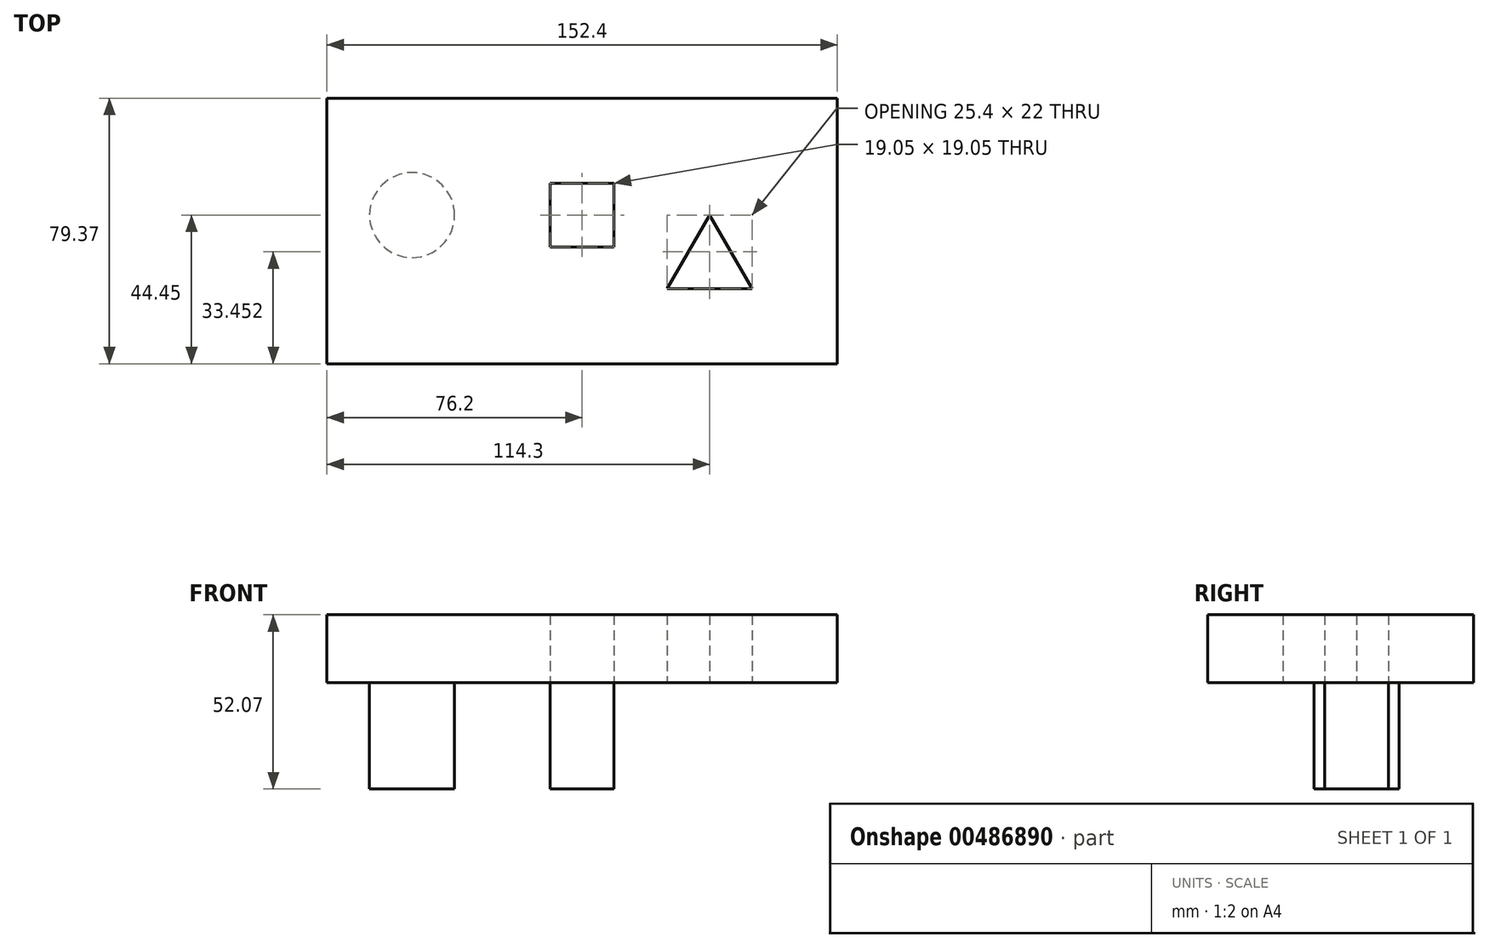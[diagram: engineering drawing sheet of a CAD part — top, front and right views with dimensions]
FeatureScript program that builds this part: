
annotation { "Feature Type Name" : "Feature", "Feature Type Description" : "" }
export const myFeature = defineFeature(function(context is Context, id is Id, definition is map)
    precondition{}
    {
        {
            var Q0;
            Q0=qCreatedBy(makeId("Top.planeOp"),FACE);
            var sketch = newSketch(context, id + "F0", { "sketchPlane" : qUnion([Q0])});
            skLineSegment(sketch, "E0", {"start": v(0, -44.45) * mm, "end": v(44.45, -44.45) * mm});
            skLineSegment(sketch, "E1.bottom", {"start": v(44.45, -44.45) * mm, "end": v(-107.95, -44.45) * mm});
            skLineSegment(sketch, "E1.top", {"start": v(44.45, 34.92) * mm, "end": v(-107.95, 34.92) * mm});
            skLineSegment(sketch, "E1.left", {"start": v(44.45, -44.45) * mm, "end": v(44.45, 34.92) * mm});
            skLineSegment(sketch, "E1.right", {"start": v(-107.95, -44.45) * mm, "end": v(-107.95, 34.92) * mm});
            skLineSegment(sketch, "E2", {"start": v(0, 0) * mm, "end": v(6.35, 0) * mm});
            skLineSegment(sketch, "E3", {"start": v(6.35, 0) * mm, "end": v(-6.35, -22) * mm});
            skLineSegment(sketch, "E4", {"start": v(-6.35, -22) * mm, "end": v(19.05, -22) * mm});
            skLineSegment(sketch, "E5", {"start": v(19.05, -22) * mm, "end": v(6.35, 0) * mm});
            skLineSegment(sketch, "E6", {"start": v(0, 0) * mm, "end": v(-31.75, 0) * mm});
            skLineSegment(sketch, "E7.bottom", {"start": v(-22.22, 9.53) * mm, "end": v(-41.27, 9.53) * mm});
            skLineSegment(sketch, "E7.top", {"start": v(-22.22, -9.53) * mm, "end": v(-41.27, -9.52) * mm});
            skLineSegment(sketch, "E7.left", {"start": v(-22.22, 9.53) * mm, "end": v(-22.22, -9.52) * mm});
            skLineSegment(sketch, "E7.right", {"start": v(-41.27, 9.53) * mm, "end": v(-41.27, -9.52) * mm});
            skPoint(sketch, "E7.middle", {"position": v(-31.75, 0) * mm});
            skCircle(sketch, "E8", {"center": v(-82.55, 0) * mm, "radius": 12.7 * mm});
            skSolve(sketch);
        }
        {
            var Q0;
            Q0=makeQuery(id+"F0.imprint","IMPRINT",FACE,{"disambiguationData":[TD([[makeQuery(id+"F0.imprint","IMPRINT",EDGE,{"derivedFrom":sQuery(id+"F0.wireOp",EDGE,"E1.top")}),1.0]])]});
            var Q1;
            Q1=makeQuery(id+"F0.imprint","IMPRINT",FACE,{"disambiguationData":[TD([[makeQuery(id+"F0.imprint","IMPRINT",EDGE,{"derivedFrom":sQuery(id+"F0.wireOp",EDGE,"E8")}),1.0]])]});
            extrude(context, id + "F1", {"entities" : qUnion([Q0, Q1]), "depth" : 20.32 * mm});
        }
        {
            var Q0;
            Q0=makeQuery(id+"F0.imprint","IMPRINT",FACE,{"disambiguationData":[TD([[makeQuery(id+"F0.imprint","IMPRINT",EDGE,{"derivedFrom":sQuery(id+"F0.wireOp",EDGE,"E8")}),1.0]])]});
            extrude(context, id + "F2", {"entities" : qUnion([Q0]), "operationType" : NewBodyOperationType.ADD, "oppositeDirection" : true, "depth" : 31.75 * mm});
        }
        {
            var Q0;
            {var subQ3=sQuery(id+"F0.wireOp",EDGE,"E7.bottom");Q0=makeQuery(id+"F0.imprint","IMPRINT",FACE,{"disambiguationData":[TD([[makeQuery(id+"F0.imprint","IMPRINT",EDGE,{"derivedFrom":subQ3}),1.0]])]});}
            extrude(context, id + "F3", {"entities" : qUnion([Q0]), "oppositeDirection" : true, "depth" : 31.75 * mm});
        }
    });
